# Revit family: НЕВАТОМ_Фильтр-бокс D FVGU, Версия 2
name_source: partatom
category: Арматура воздуховодов
revit_build: Autodesk Revit 2017 (Build: 20170118_1100(x64)
units: mm (PartAtom-declared; Revit-internal decimal feet)

## family parameters
Всегда вертикально = Нет
На основе рабочей плоскости = Нет
Общий = Нет
При загрузке вырезать с полостями = Нет
Размер круглого соединителя = Использовать диаметр
Тип детали = Вставляется

## types (9) — shared parameters
ADSK_Единица измерения = шт.
ADSK_Завод-изготовитель = НЕВАТОМ
ADSK_Количество = 1
ADSK_Материал наименование = Оцинкованная сталь
ADSK_Потеря давления воздуха = 0.0 Па
Nevatom_URL = https://t.me
Материал = Сталь оцинкованная

## per-type parameters (varying)
| type | A | ADSK_Марка | ADSK_Расход воздуха | B | L |
| Фильтр-бокс FVGU-100 | 200 мм | FVGU-100 | 70.0 м³/ч | 202 мм | 100 мм |
| Фильтр-бокс FVGU-125 | 200 мм | FVGU-125 | 110.0 м³/ч | 202 мм | 180 мм |
| Фильтр-бокс FVGU-160 | 200 мм | FVGU-160 | 180.0 м³/ч | 202 мм | 180 мм |
| Фильтр-бокс FVGU-200 | 244 мм | FVGU-200 | 280.0 м³/ч | 246 мм | 180 мм |
| Фильтр-бокс FVGU-250 | 294 мм | FVGU-250 | 440.0 м³/ч | 296 мм | 180 мм |
| Фильтр-бокс FVGU-315 | 343 мм | FVGU-315 | 700.0 м³/ч | 345 мм | 180 мм |
| Фильтр-бокс FVGU-355 | 393 мм | FVGU-355 | 850.0 м³/ч | 395 мм | 140 мм |
| Фильтр-бокс FVGU-400 | 448 мм | FVGU-400 | 1100.0 м³/ч | 450 мм | 140 мм |
| Фильтр-бокс FVGU-500 | 550 мм | FVGU-500 | 1750.0 м³/ч | 556 мм | 140 мм |
